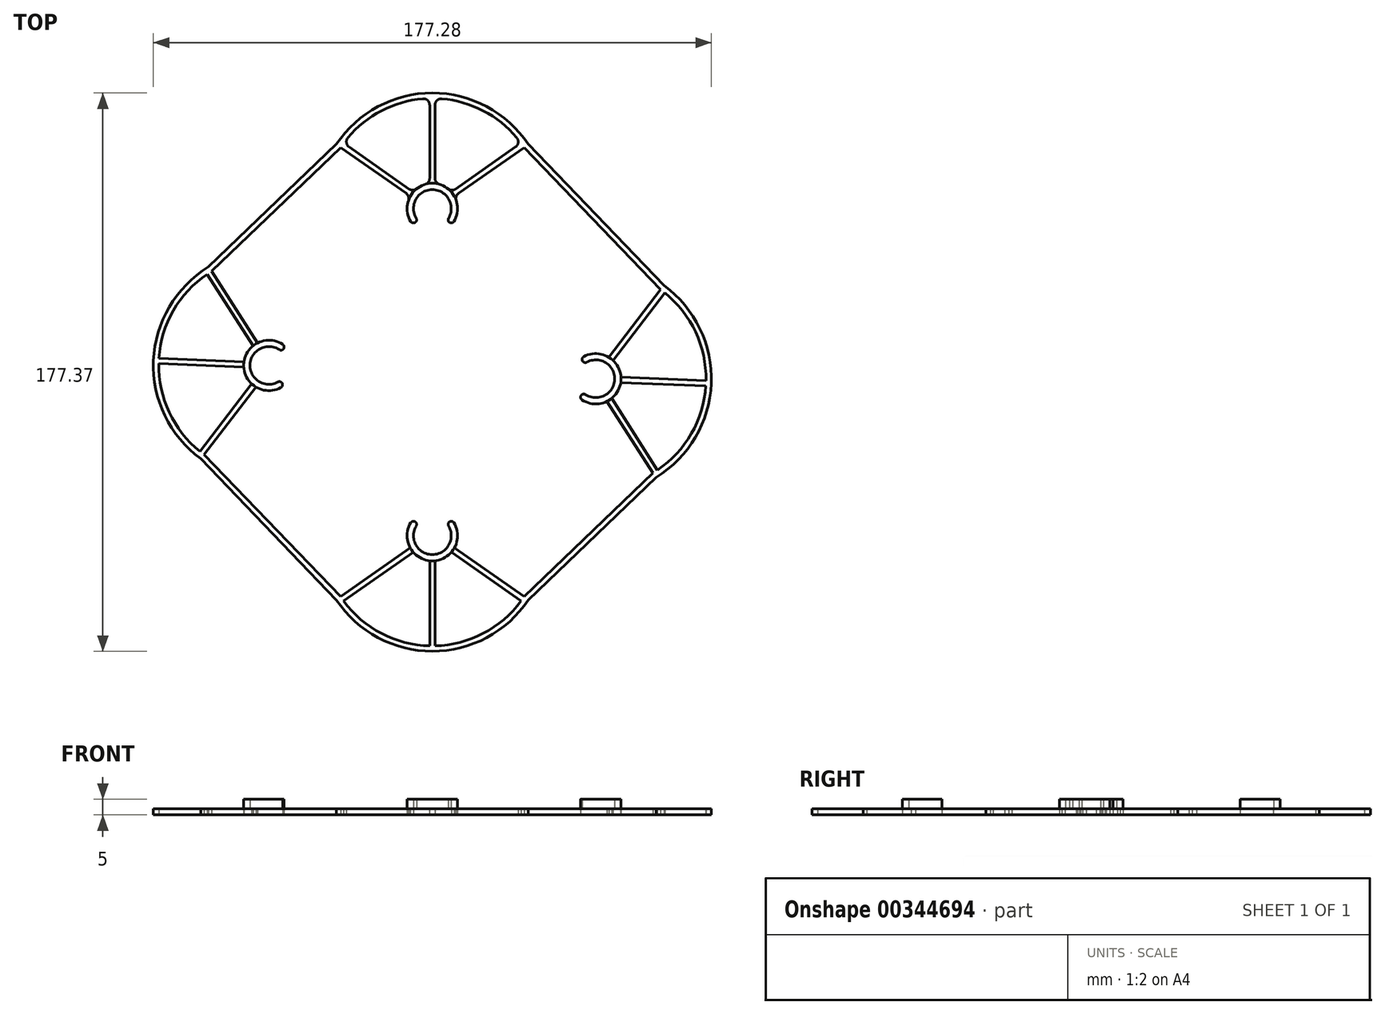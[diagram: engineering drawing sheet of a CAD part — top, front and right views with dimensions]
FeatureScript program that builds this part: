
annotation { "Feature Type Name" : "Feature", "Feature Type Description" : "" }
export const myFeature = defineFeature(function(context is Context, id is Id, definition is map)
    precondition{}
    {
        {
            var Q0;
            Q0=qCreatedBy(makeId("Top.planeOp"),FACE);
            var sketch = newSketch(context, id + "F0", { "sketchPlane" : qUnion([Q0])});
            skArc(sketch, "E0", {"start": v(5, -3.32) * mm, "mid": v(0, 6) * mm, "end": v(-5, -3.32) * mm});
            skArc(sketch, "E1", {"start": v(-7, 3.87) * mm, "mid": v(-7.85, -1.56) * mm, "end": v(-5, -6.24) * mm});
            skLineSegment(sketch, "E2", {"start": v(-7, 3.87) * mm, "end": v(-29.15, 19.37) * mm});
            skArc(sketch, "E3", {"start": v(28.17, 20.77) * mm, "mid": v(16.16, 31.05) * mm, "end": v(0.85, 34.99) * mm});
            skLineSegment(sketch, "E4", {"start": v(-6.03, 5.26) * mm, "end": v(-28.17, 20.77) * mm});
            skLineSegment(sketch, "E5", {"start": v(0, 0) * mm, "end": v(-28.67, 20.08) * mm, "construction": true});
            skLineSegment(sketch, "E6", {"start": v(0, 0) * mm, "end": v(0, 35) * mm, "construction": true});
            skLineSegment(sketch, "E7.MirrorCS", {"start": v(6.03, 5.26) * mm, "end": v(28.17, 20.77) * mm});
            skLineSegment(sketch, "E8.MirrorCS", {"start": v(7, 3.87) * mm, "end": v(29.15, 19.37) * mm});
            skLineSegment(sketch, "E9", {"start": v(-0.85, 7.95) * mm, "end": v(-0.85, 34.99) * mm});
            skLineSegment(sketch, "E10", {"start": v(0.85, 34.99) * mm, "end": v(0.85, 7.95) * mm});
            skArc(sketch, "E11", {"start": v(30.49, 20.43) * mm, "mid": v(0, 36.7) * mm, "end": v(-30.49, 20.43) * mm});
            skArc(sketch, "E12.trimOffspring", {"start": v(-0.85, 7.95) * mm, "mid": v(-3.7, 7.1) * mm, "end": v(-6.03, 5.26) * mm});
            skArc(sketch, "E13.trimOffspring", {"start": v(6.03, 5.26) * mm, "mid": v(3.7, 7.1) * mm, "end": v(0.85, 7.95) * mm});
            skArc(sketch, "E14.trimOffspring", {"start": v(-0.85, 34.99) * mm, "mid": v(-16.16, 31.05) * mm, "end": v(-28.17, 20.77) * mm});
            skPoint(sketch, "E15.middle", {"position": v(0, -9.2) * mm});
            skPoint(sketch, "E15.bottom.start.orphan", {"position": v(-4, -0.06) * mm});
            skPoint(sketch, "E16.orphan", {"position": v(4, 0.05) * mm});
            skArc(sketch, "E17.trimOffspring", {"start": v(5, -6.24) * mm, "mid": v(7.85, -1.56) * mm, "end": v(7, 3.87) * mm});
            skPoint(sketch, "E15.top.end.orphan", {"position": v(4, -18.32) * mm});
            skPoint(sketch, "E15.top.start.orphan", {"position": v(-4, -18.43) * mm});
            skLineSegment(sketch, "E18", {"start": v(0, 0) * mm, "end": v(51.94, -54.1) * mm, "construction": true});
            skLineSegment(sketch, "E19", {"start": v(51.94, -54.1) * mm, "end": v(0, -103.97) * mm, "construction": true});
            skLineSegment(sketch, "E20", {"start": v(0, -103.97) * mm, "end": v(-51.94, -49.86) * mm, "construction": true});
            skLineSegment(sketch, "E21", {"start": v(-51.94, -49.86) * mm, "end": v(0, 0) * mm, "construction": true});
            skLineSegment(sketch, "E22", {"start": v(0, 0) * mm, "end": v(0, -103.97) * mm, "construction": true});
            skLineSegment(sketch, "E23", {"start": v(51.94, -54.1) * mm, "end": v(-51.94, -49.86) * mm, "construction": true});
            skLineSegment(sketch, "E24", {"start": v(0, -51.98) * mm, "end": v(54.15, 0) * mm, "construction": true});
            skLineSegment(sketch, "E25.MirrorCS", {"start": v(48.42, -58.96) * mm, "end": v(45.5, -58.85) * mm});
            skLineSegment(sketch, "E26.MirrorCS", {"start": v(48.83, -48.97) * mm, "end": v(45.9, -48.85) * mm});
            skArc(sketch, "E27.MirrorCS", {"start": v(57.44, -48.3) * mm, "mid": v(59.18, -50.7) * mm, "end": v(59.92, -53.58) * mm});
            skArc(sketch, "E28.MirrorCS", {"start": v(59.85, -55.28) * mm, "mid": v(58.88, -58.08) * mm, "end": v(56.95, -60.34) * mm});
            skLineSegment(sketch, "E29.MirrorCS", {"start": v(55.52, -61.26) * mm, "end": v(70.1, -84.02) * mm});
            skLineSegment(sketch, "E30.MirrorCS", {"start": v(57.44, -48.3) * mm, "end": v(73.84, -26.8) * mm});
            skArc(sketch, "E31.MirrorCS", {"start": v(55.52, -61.26) * mm, "mid": v(50.07, -61.88) * mm, "end": v(45.5, -58.85) * mm});
            skPoint(sketch, "E32.MirrorP", {"position": v(51.71, -58.1) * mm});
            skLineSegment(sketch, "E33.MirrorCS", {"start": v(56.09, -47.26) * mm, "end": v(72.49, -25.77) * mm});
            skLineSegment(sketch, "E34.MirrorCS", {"start": v(56.95, -60.34) * mm, "end": v(71.54, -83.1) * mm});
            skArc(sketch, "E35.MirrorCS", {"start": v(73.6, -24.47) * mm, "mid": v(88.6, -55.6) * mm, "end": v(71.1, -85.4) * mm});
            skArc(sketch, "E36.MirrorCS", {"start": v(73.84, -26.8) * mm, "mid": v(83.62, -39.22) * mm, "end": v(86.94, -54.68) * mm});
            skLineSegment(sketch, "E37.MirrorCS", {"start": v(59.85, -55.28) * mm, "end": v(86.87, -56.38) * mm});
            skLineSegment(sketch, "E38.MirrorCS", {"start": v(86.94, -54.68) * mm, "end": v(59.92, -53.58) * mm});
            skArc(sketch, "E39.MirrorCS", {"start": v(48.83, -48.97) * mm, "mid": v(57.93, -54.35) * mm, "end": v(48.42, -58.96) * mm});
            skPoint(sketch, "E40.MirrorP", {"position": v(52.15, -50.1) * mm});
            skArc(sketch, "E41.MirrorCS", {"start": v(45.9, -48.85) * mm, "mid": v(50.7, -46.2) * mm, "end": v(56.09, -47.26) * mm});
            skArc(sketch, "E42.MirrorCS", {"start": v(86.87, -56.38) * mm, "mid": v(82.3, -71.52) * mm, "end": v(71.54, -83.1) * mm});
            skLineSegment(sketch, "E43", {"start": v(0, -51.98) * mm, "end": v(-83.37, 34.86) * mm, "construction": true});
            skArc(sketch, "E44.MirrorCS", {"start": v(-45.9, -55.11) * mm, "mid": v(-50.7, -57.77) * mm, "end": v(-56.09, -56.7) * mm});
            skLineSegment(sketch, "E45.MirrorCS", {"start": v(-48.83, -55) * mm, "end": v(-45.9, -55.11) * mm});
            skArc(sketch, "E46.MirrorCS", {"start": v(-57.44, -55.67) * mm, "mid": v(-59.18, -53.26) * mm, "end": v(-59.92, -50.39) * mm});
            skLineSegment(sketch, "E47.MirrorCS", {"start": v(-48.42, -45) * mm, "end": v(-45.5, -45.12) * mm});
            skArc(sketch, "E48.MirrorCS", {"start": v(-73.6, -79.5) * mm, "mid": v(-88.6, -48.36) * mm, "end": v(-71.1, -18.57) * mm});
            skArc(sketch, "E49.MirrorCS", {"start": v(-59.85, -48.69) * mm, "mid": v(-58.88, -45.88) * mm, "end": v(-56.95, -43.62) * mm});
            skArc(sketch, "E50.MirrorCS", {"start": v(-73.84, -77.17) * mm, "mid": v(-83.62, -64.74) * mm, "end": v(-86.94, -49.28) * mm});
            skPoint(sketch, "E51.MirrorP", {"position": v(-52.15, -53.86) * mm});
            skArc(sketch, "E52.MirrorCS", {"start": v(-86.87, -47.59) * mm, "mid": v(-82.3, -32.45) * mm, "end": v(-71.54, -20.86) * mm});
            skLineSegment(sketch, "E53.MirrorCS", {"start": v(-59.85, -48.69) * mm, "end": v(-86.87, -47.59) * mm});
            skPoint(sketch, "E54.MirrorP", {"position": v(-42.76, -50.24) * mm});
            skArc(sketch, "E55.MirrorCS", {"start": v(-48.83, -55) * mm, "mid": v(-57.93, -49.62) * mm, "end": v(-48.42, -45) * mm});
            skLineSegment(sketch, "E56.MirrorCS", {"start": v(-56.95, -43.62) * mm, "end": v(-71.54, -20.86) * mm});
            skArc(sketch, "E57.MirrorCS", {"start": v(-55.52, -42.7) * mm, "mid": v(-50.07, -42.08) * mm, "end": v(-45.5, -45.12) * mm});
            skLineSegment(sketch, "E58.MirrorCS", {"start": v(-56.09, -56.7) * mm, "end": v(-72.49, -78.2) * mm});
            skLineSegment(sketch, "E59.MirrorCS", {"start": v(-55.52, -42.7) * mm, "end": v(-70.1, -19.95) * mm});
            skPoint(sketch, "E60.MirrorP", {"position": v(-51.71, -45.87) * mm});
            skLineSegment(sketch, "E61.MirrorCS", {"start": v(-57.44, -55.67) * mm, "end": v(-73.84, -77.17) * mm});
            skLineSegment(sketch, "E62.MirrorCS", {"start": v(-86.94, -49.28) * mm, "end": v(-59.92, -50.39) * mm});
            skLineSegment(sketch, "E63.MirrorCS", {"start": v(-5, -100.65) * mm, "end": v(-5, -97.72) * mm});
            skArc(sketch, "E64.MirrorCS", {"start": v(0.85, -111.92) * mm, "mid": v(3.7, -111.06) * mm, "end": v(6.03, -109.23) * mm});
            skArc(sketch, "E65.MirrorCS", {"start": v(-6.03, -109.23) * mm, "mid": v(-3.7, -111.06) * mm, "end": v(-0.85, -111.92) * mm});
            skLineSegment(sketch, "E66.MirrorCS", {"start": v(5, -100.65) * mm, "end": v(5, -97.72) * mm});
            skLineSegment(sketch, "E67.MirrorCS", {"start": v(-6.03, -109.23) * mm, "end": v(-28.17, -124.73) * mm});
            skArc(sketch, "E68.MirrorCS", {"start": v(-30.49, -124.4) * mm, "mid": v(0, -140.67) * mm, "end": v(30.49, -124.4) * mm});
            skArc(sketch, "E69.MirrorCS", {"start": v(-5, -97.72) * mm, "mid": v(-7.85, -102.41) * mm, "end": v(-7, -107.83) * mm});
            skArc(sketch, "E70.MirrorCS", {"start": v(-5, -100.65) * mm, "mid": v(0, -109.97) * mm, "end": v(5, -100.65) * mm});
            skArc(sketch, "E71.MirrorCS", {"start": v(-28.17, -124.73) * mm, "mid": v(-16.16, -135.01) * mm, "end": v(-0.85, -138.96) * mm});
            skPoint(sketch, "E72.MirrorP", {"position": v(-4, -104.01) * mm});
            skLineSegment(sketch, "E73.MirrorCS", {"start": v(-7, -107.83) * mm, "end": v(-29.15, -123.34) * mm});
            skLineSegment(sketch, "E74.MirrorCS", {"start": v(0.85, -111.92) * mm, "end": v(0.85, -138.96) * mm});
            skArc(sketch, "E75.MirrorCS", {"start": v(7, -107.83) * mm, "mid": v(7.85, -102.41) * mm, "end": v(5, -97.72) * mm});
            skPoint(sketch, "E76.MirrorP", {"position": v(4, -103.9) * mm});
            skLineSegment(sketch, "E77.MirrorCS", {"start": v(-0.85, -138.96) * mm, "end": v(-0.85, -111.92) * mm});
            skLineSegment(sketch, "E78.MirrorCS", {"start": v(7, -107.83) * mm, "end": v(29.15, -123.34) * mm});
            skLineSegment(sketch, "E79.MirrorCS", {"start": v(6.03, -109.23) * mm, "end": v(28.17, -124.73) * mm});
            skArc(sketch, "E80.MirrorCS", {"start": v(0.85, -138.96) * mm, "mid": v(16.16, -135.01) * mm, "end": v(28.17, -124.73) * mm});
            skLineSegment(sketch, "E81", {"start": v(73.6, -24.47) * mm, "end": v(30.49, 20.43) * mm});
            skLineSegment(sketch, "E82", {"start": v(72.49, -25.77) * mm, "end": v(29.15, 19.37) * mm});
            skLineSegment(sketch, "E83", {"start": v(71.1, -85.4) * mm, "end": v(30.49, -124.4) * mm});
            skLineSegment(sketch, "E84", {"start": v(70.1, -84.02) * mm, "end": v(29.15, -123.34) * mm});
            skLineSegment(sketch, "E85", {"start": v(-30.49, -124.4) * mm, "end": v(-73.6, -79.5) * mm});
            skLineSegment(sketch, "E86", {"start": v(-29.15, -123.34) * mm, "end": v(-72.49, -78.2) * mm});
            skLineSegment(sketch, "E87", {"start": v(-71.1, -18.57) * mm, "end": v(-30.49, 20.43) * mm});
            skLineSegment(sketch, "E88", {"start": v(-29.15, 19.37) * mm, "end": v(-70.1, -19.95) * mm});
            skLineSegment(sketch, "E89", {"start": v(-5, -3.32) * mm, "end": v(-5, -6.24) * mm});
            skLineSegment(sketch, "E90", {"start": v(5, -3.32) * mm, "end": v(5, -6.24) * mm});
            skSolve(sketch);
        }
        {
            var Q0;
            Q0 = qSketchRegion(id + "F0", true);
            extrude(context, id + "F1", {"entities" : qUnion([Q0]), "depth" : 2 * mm});
        }
        {
            var Q0;
            Q0=makeQuery(id+"F1.opExtrude","SWEPT_EDGE",EDGE,{"disambiguationData":[OSD([sQuery(id+"F0.wireOp",EDGE,"E0"),sQuery(id+"F0.wireOp",EDGE,"E89")])]});
            var Q1;
            Q1=makeQuery(id+"F1.opExtrude","SWEPT_EDGE",EDGE,{"disambiguationData":[OSD([sQuery(id+"F0.wireOp",EDGE,"E1"),sQuery(id+"F0.wireOp",EDGE,"E89")])]});
            var Q2;
            Q2=makeQuery(id+"F1.opExtrude","SWEPT_EDGE",EDGE,{"disambiguationData":[OSD([sQuery(id+"F0.wireOp",EDGE,"E0"),sQuery(id+"F0.wireOp",EDGE,"E90")])]});
            var Q3;
            Q3=makeQuery(id+"F1.opExtrude","SWEPT_EDGE",EDGE,{"disambiguationData":[OSD([sQuery(id+"F0.wireOp",EDGE,"E17.trimOffspring"),sQuery(id+"F0.wireOp",EDGE,"E90")])]});
            var Q4;
            Q4=makeQuery(id+"F1.opExtrude","SWEPT_EDGE",EDGE,{"disambiguationData":[OSD([sQuery(id+"F0.wireOp",EDGE,"E26.MirrorCS"),sQuery(id+"F0.wireOp",EDGE,"E39.MirrorCS")])]});
            var Q5;
            Q5=makeQuery(id+"F1.opExtrude","SWEPT_EDGE",EDGE,{"disambiguationData":[OSD([sQuery(id+"F0.wireOp",EDGE,"E26.MirrorCS"),sQuery(id+"F0.wireOp",EDGE,"E41.MirrorCS")])]});
            var Q6;
            Q6=makeQuery(id+"F1.opExtrude","SWEPT_EDGE",EDGE,{"disambiguationData":[OSD([sQuery(id+"F0.wireOp",EDGE,"E25.MirrorCS"),sQuery(id+"F0.wireOp",EDGE,"E39.MirrorCS")])]});
            var Q7;
            Q7=makeQuery(id+"F1.opExtrude","SWEPT_EDGE",EDGE,{"disambiguationData":[OSD([sQuery(id+"F0.wireOp",EDGE,"E25.MirrorCS"),sQuery(id+"F0.wireOp",EDGE,"E31.MirrorCS")])]});
            var Q8;
            Q8=makeQuery(id+"F1.opExtrude","SWEPT_EDGE",EDGE,{"disambiguationData":[OSD([sQuery(id+"F0.wireOp",EDGE,"E66.MirrorCS"),sQuery(id+"F0.wireOp",EDGE,"E70.MirrorCS")])]});
            var Q9;
            Q9=makeQuery(id+"F1.opExtrude","SWEPT_EDGE",EDGE,{"disambiguationData":[OSD([sQuery(id+"F0.wireOp",EDGE,"E66.MirrorCS"),sQuery(id+"F0.wireOp",EDGE,"E75.MirrorCS")])]});
            var Q10;
            Q10=makeQuery(id+"F1.opExtrude","SWEPT_EDGE",EDGE,{"disambiguationData":[OSD([sQuery(id+"F0.wireOp",EDGE,"E63.MirrorCS"),sQuery(id+"F0.wireOp",EDGE,"E69.MirrorCS")])]});
            var Q11;
            Q11=makeQuery(id+"F1.opExtrude","SWEPT_EDGE",EDGE,{"disambiguationData":[OSD([sQuery(id+"F0.wireOp",EDGE,"E63.MirrorCS"),sQuery(id+"F0.wireOp",EDGE,"E70.MirrorCS")])]});
            var Q12;
            Q12=makeQuery(id+"F1.opExtrude","SWEPT_EDGE",EDGE,{"disambiguationData":[OSD([sQuery(id+"F0.wireOp",EDGE,"E45.MirrorCS"),sQuery(id+"F0.wireOp",EDGE,"E55.MirrorCS")])]});
            var Q13;
            Q13=makeQuery(id+"F1.opExtrude","SWEPT_EDGE",EDGE,{"disambiguationData":[OSD([sQuery(id+"F0.wireOp",EDGE,"E44.MirrorCS"),sQuery(id+"F0.wireOp",EDGE,"E45.MirrorCS")])]});
            var Q14;
            Q14=makeQuery(id+"F1.opExtrude","SWEPT_EDGE",EDGE,{"disambiguationData":[OSD([sQuery(id+"F0.wireOp",EDGE,"E47.MirrorCS"),sQuery(id+"F0.wireOp",EDGE,"E55.MirrorCS")])]});
            var Q15;
            Q15=makeQuery(id+"F1.opExtrude","SWEPT_EDGE",EDGE,{"disambiguationData":[OSD([sQuery(id+"F0.wireOp",EDGE,"E47.MirrorCS"),sQuery(id+"F0.wireOp",EDGE,"E57.MirrorCS")])]});
            fillet(context, id + "F2", {"entities" : qUnion([Q0, Q1, Q2, Q3, Q4, Q5, Q6, Q7, Q8, Q9, Q10, Q11, Q12, Q13, Q14, Q15]), "radius" : 1 * mm, "tangentPropagation" : true, "allowEdgeOverflow" : false});
        }
        {
            var Q0;
            Q0=makeQuery(id+"F1.opExtrude","SWEPT_EDGE",EDGE,{"disambiguationData":[OSD([sQuery(id+"F0.wireOp",EDGE,"E7.MirrorCS"),sQuery(id+"F0.wireOp",EDGE,"E13.trimOffspring")])]});
            var Q1;
            Q1=makeQuery(id+"F1.opExtrude","SWEPT_EDGE",EDGE,{"disambiguationData":[OSD([sQuery(id+"F0.wireOp",EDGE,"E10"),sQuery(id+"F0.wireOp",EDGE,"E13.trimOffspring")])]});
            var Q2;
            Q2=makeQuery(id+"F1.opExtrude","SWEPT_EDGE",EDGE,{"disambiguationData":[OSD([sQuery(id+"F0.wireOp",EDGE,"E8.MirrorCS"),sQuery(id+"F0.wireOp",EDGE,"E17.trimOffspring")])]});
            var Q3;
            Q3=makeQuery(id+"F1.opExtrude","SWEPT_EDGE",EDGE,{"disambiguationData":[OSD([sQuery(id+"F0.wireOp",EDGE,"E9"),sQuery(id+"F0.wireOp",EDGE,"E12.trimOffspring")])]});
            var Q4;
            Q4=makeQuery(id+"F1.opExtrude","SWEPT_EDGE",EDGE,{"disambiguationData":[OSD([sQuery(id+"F0.wireOp",EDGE,"E1"),sQuery(id+"F0.wireOp",EDGE,"E2")])]});
            var Q5;
            Q5=makeQuery(id+"F1.opExtrude","SWEPT_EDGE",EDGE,{"disambiguationData":[OSD([sQuery(id+"F0.wireOp",EDGE,"E4"),sQuery(id+"F0.wireOp",EDGE,"E12.trimOffspring")])]});
            var Q6;
            Q6=makeQuery(id+"F1.opExtrude","SWEPT_EDGE",EDGE,{"disambiguationData":[OSD([sQuery(id+"F0.wireOp",EDGE,"E3"),sQuery(id+"F0.wireOp",EDGE,"E7.MirrorCS")])]});
            var Q7;
            Q7=makeQuery(id+"F1.opExtrude","SWEPT_EDGE",EDGE,{"disambiguationData":[OSD([sQuery(id+"F0.wireOp",EDGE,"E4"),sQuery(id+"F0.wireOp",EDGE,"E14.trimOffspring")])]});
            var Q8;
            Q8=makeQuery(id+"F1.opExtrude","SWEPT_EDGE",EDGE,{"disambiguationData":[OSD([sQuery(id+"F0.wireOp",EDGE,"E9"),sQuery(id+"F0.wireOp",EDGE,"E14.trimOffspring")])]});
            var Q9;
            Q9=makeQuery(id+"F1.opExtrude","SWEPT_EDGE",EDGE,{"disambiguationData":[OSD([sQuery(id+"F0.wireOp",EDGE,"E3"),sQuery(id+"F0.wireOp",EDGE,"E10")])]});
            fillet(context, id + "F3", {"entities" : qUnion([Q0, Q1, Q2, Q3, Q4, Q5, Q6, Q7, Q8, Q9]), "radius" : 2 * mm, "tangentPropagation" : true, "allowEdgeOverflow" : false});
        }
        {
            var Q0;
            Q0=makeQuery(id+"F1.opExtrude","CAP_FACE",FACE,{"disambiguationData":[OSD([sQuery(id+"F0.wireOp",EDGE,"E0"),sQuery(id+"F0.wireOp",EDGE,"E1"),sQuery(id+"F0.wireOp",EDGE,"E2"),sQuery(id+"F0.wireOp",EDGE,"E3"),sQuery(id+"F0.wireOp",EDGE,"E4"),sQuery(id+"F0.wireOp",EDGE,"E7.MirrorCS"),sQuery(id+"F0.wireOp",EDGE,"E8.MirrorCS"),sQuery(id+"F0.wireOp",EDGE,"E9"),sQuery(id+"F0.wireOp",EDGE,"E10"),sQuery(id+"F0.wireOp",EDGE,"E11"),sQuery(id+"F0.wireOp",EDGE,"E12.trimOffspring"),sQuery(id+"F0.wireOp",EDGE,"E13.trimOffspring"),sQuery(id+"F0.wireOp",EDGE,"E14.trimOffspring"),sQuery(id+"F0.wireOp",EDGE,"E15.left"),sQuery(id+"F0.wireOp",EDGE,"E15.right"),sQuery(id+"F0.wireOp",EDGE,"E17.trimOffspring"),sQuery(id+"F0.wireOp",EDGE,"E25.MirrorCS"),sQuery(id+"F0.wireOp",EDGE,"E26.MirrorCS"),sQuery(id+"F0.wireOp",EDGE,"E27.MirrorCS"),sQuery(id+"F0.wireOp",EDGE,"E28.MirrorCS"),sQuery(id+"F0.wireOp",EDGE,"E29.MirrorCS"),sQuery(id+"F0.wireOp",EDGE,"E30.MirrorCS"),sQuery(id+"F0.wireOp",EDGE,"E31.MirrorCS"),sQuery(id+"F0.wireOp",EDGE,"E33.MirrorCS"),sQuery(id+"F0.wireOp",EDGE,"E34.MirrorCS"),sQuery(id+"F0.wireOp",EDGE,"E35.MirrorCS"),sQuery(id+"F0.wireOp",EDGE,"E36.MirrorCS"),sQuery(id+"F0.wireOp",EDGE,"E37.MirrorCS"),sQuery(id+"F0.wireOp",EDGE,"E38.MirrorCS"),sQuery(id+"F0.wireOp",EDGE,"E39.MirrorCS"),sQuery(id+"F0.wireOp",EDGE,"E41.MirrorCS"),sQuery(id+"F0.wireOp",EDGE,"E42.MirrorCS"),sQuery(id+"F0.wireOp",EDGE,"E44.MirrorCS"),sQuery(id+"F0.wireOp",EDGE,"E45.MirrorCS"),sQuery(id+"F0.wireOp",EDGE,"E46.MirrorCS"),sQuery(id+"F0.wireOp",EDGE,"E47.MirrorCS"),sQuery(id+"F0.wireOp",EDGE,"E48.MirrorCS"),sQuery(id+"F0.wireOp",EDGE,"E49.MirrorCS"),sQuery(id+"F0.wireOp",EDGE,"E50.MirrorCS"),sQuery(id+"F0.wireOp",EDGE,"E52.MirrorCS"),sQuery(id+"F0.wireOp",EDGE,"E53.MirrorCS"),sQuery(id+"F0.wireOp",EDGE,"E55.MirrorCS"),sQuery(id+"F0.wireOp",EDGE,"E56.MirrorCS"),sQuery(id+"F0.wireOp",EDGE,"E57.MirrorCS"),sQuery(id+"F0.wireOp",EDGE,"E58.MirrorCS"),sQuery(id+"F0.wireOp",EDGE,"E59.MirrorCS"),sQuery(id+"F0.wireOp",EDGE,"E61.MirrorCS"),sQuery(id+"F0.wireOp",EDGE,"E62.MirrorCS"),sQuery(id+"F0.wireOp",EDGE,"E63.MirrorCS"),sQuery(id+"F0.wireOp",EDGE,"E64.MirrorCS"),sQuery(id+"F0.wireOp",EDGE,"E65.MirrorCS"),sQuery(id+"F0.wireOp",EDGE,"E66.MirrorCS"),sQuery(id+"F0.wireOp",EDGE,"E67.MirrorCS"),sQuery(id+"F0.wireOp",EDGE,"E68.MirrorCS"),sQuery(id+"F0.wireOp",EDGE,"E69.MirrorCS"),sQuery(id+"F0.wireOp",EDGE,"E70.MirrorCS"),sQuery(id+"F0.wireOp",EDGE,"E71.MirrorCS"),sQuery(id+"F0.wireOp",EDGE,"E73.MirrorCS"),sQuery(id+"F0.wireOp",EDGE,"E74.MirrorCS"),sQuery(id+"F0.wireOp",EDGE,"E75.MirrorCS"),sQuery(id+"F0.wireOp",EDGE,"E77.MirrorCS"),sQuery(id+"F0.wireOp",EDGE,"E78.MirrorCS"),sQuery(id+"F0.wireOp",EDGE,"E79.MirrorCS"),sQuery(id+"F0.wireOp",EDGE,"E80.MirrorCS"),sQuery(id+"F0.wireOp",EDGE,"E81"),sQuery(id+"F0.wireOp",EDGE,"E82"),sQuery(id+"F0.wireOp",EDGE,"E83"),sQuery(id+"F0.wireOp",EDGE,"E84"),sQuery(id+"F0.wireOp",EDGE,"E85"),sQuery(id+"F0.wireOp",EDGE,"E86"),sQuery(id+"F0.wireOp",EDGE,"E87"),sQuery(id+"F0.wireOp",EDGE,"E88")])],"isStart":false});
            var sketch = newSketch(context, id + "F4", { "sketchPlane" : qUnion([Q0])});
            skLineSegment(sketch, "E91.0", {"start": v(73.6, -24.47) * mm, "end": v(30.49, 20.43) * mm});
            skArc(sketch, "E92.0", {"start": v(73.6, -24.47) * mm, "mid": v(88.6, -55.6) * mm, "end": v(71.1, -85.4) * mm});
            skLineSegment(sketch, "E93.0", {"start": v(71.1, -85.4) * mm, "end": v(30.49, -124.4) * mm});
            skArc(sketch, "E94.0", {"start": v(-30.49, -124.4) * mm, "mid": v(0, -140.67) * mm, "end": v(30.49, -124.4) * mm});
            skLineSegment(sketch, "E95.0", {"start": v(-30.49, -124.4) * mm, "end": v(-73.6, -79.5) * mm});
            skArc(sketch, "E96.0", {"start": v(-73.6, -79.5) * mm, "mid": v(-88.6, -48.36) * mm, "end": v(-71.1, -18.57) * mm});
            skLineSegment(sketch, "E97.0", {"start": v(-71.1, -18.57) * mm, "end": v(-30.49, 20.43) * mm});
            skArc(sketch, "E98.0", {"start": v(30.49, 20.43) * mm, "mid": v(0, 36.7) * mm, "end": v(-30.49, 20.43) * mm});
            skArc(sketch, "E99.0", {"start": v(72.7, -25.5) * mm, "mid": v(87.26, -55.56) * mm, "end": v(70.28, -84.33) * mm});
            skLineSegment(sketch, "E99.1", {"start": v(70.28, -84.33) * mm, "end": v(29.45, -123.52) * mm});
            skLineSegment(sketch, "E99.2", {"start": v(72.7, -25.5) * mm, "end": v(29.43, 19.58) * mm});
            skArc(sketch, "E99.3", {"start": v(-29.43, -123.55) * mm, "mid": v(0.01, -139.32) * mm, "end": v(29.45, -123.52) * mm});
            skArc(sketch, "E99.4", {"start": v(29.43, 19.58) * mm, "mid": v(-0.01, 35.35) * mm, "end": v(-29.45, 19.56) * mm});
            skLineSegment(sketch, "E99.5", {"start": v(-70.28, -19.64) * mm, "end": v(-29.45, 19.56) * mm});
            skArc(sketch, "E99.6", {"start": v(-72.7, -78.47) * mm, "mid": v(-87.26, -48.4) * mm, "end": v(-70.28, -19.64) * mm});
            skLineSegment(sketch, "E99.7", {"start": v(-29.43, -123.55) * mm, "end": v(-72.7, -78.47) * mm});
            skSolve(sketch);
        }
        {
            var Q0;
            Q0=makeQuery(id+"F4.imprint","IMPRINT",FACE,{"disambiguationData":[TD([[makeQuery(id+"F4.imprint","IMPRINT",EDGE,{"derivedFrom":sQuery(id+"F4.wireOp",EDGE,"E99.0")}),-1.0]])]});
            var sketch = newSketch(context, id + "F5", { "sketchPlane" : qUnion([Q0])});
            skArc(sketch, "E100.0", {"start": v(-49.06, -55.13) * mm, "mid": v(-57.93, -49.62) * mm, "end": v(-48.64, -44.85) * mm, "construction": true});
            skArc(sketch, "E101.0", {"start": v(-48.64, -44.85) * mm, "mid": v(-47.26, -44.56) * mm, "end": v(-47.54, -43.18) * mm});
            skPoint(sketch, "E102.0", {"position": v(-48.1, -56.88) * mm});
            skArc(sketch, "E103.0", {"start": v(-48.1, -56.88) * mm, "mid": v(-47.7, -55.52) * mm, "end": v(-49.06, -55.13) * mm});
            skArc(sketch, "E104.0", {"start": v(-5.14, -100.88) * mm, "mid": v(0, -109.97) * mm, "end": v(5.14, -100.88) * mm, "construction": true});
            skArc(sketch, "E105.0", {"start": v(6.86, -99.85) * mm, "mid": v(5.48, -99.5) * mm, "end": v(5.14, -100.88) * mm});
            skArc(sketch, "E106.0", {"start": v(-5.14, -100.88) * mm, "mid": v(-5.48, -99.5) * mm, "end": v(-6.86, -99.85) * mm});
            skArc(sketch, "E107.0", {"start": v(49.06, -48.84) * mm, "mid": v(57.93, -54.35) * mm, "end": v(48.64, -59.12) * mm, "construction": true});
            skArc(sketch, "E108.0", {"start": v(48.64, -59.12) * mm, "mid": v(47.26, -59.4) * mm, "end": v(47.54, -60.79) * mm});
            skArc(sketch, "E109.0", {"start": v(48.1, -47.08) * mm, "mid": v(47.7, -48.44) * mm, "end": v(49.06, -48.84) * mm});
            skArc(sketch, "E110.0", {"start": v(5.14, -3.1) * mm, "mid": v(0, 6) * mm, "end": v(-5.14, -3.1) * mm, "construction": true});
            skArc(sketch, "E111.0", {"start": v(5.14, -3.1) * mm, "mid": v(5.48, -4.46) * mm, "end": v(6.86, -4.12) * mm});
            skArc(sketch, "E112.0", {"start": v(-6.86, -4.12) * mm, "mid": v(-5.48, -4.46) * mm, "end": v(-5.14, -3.1) * mm});
            skArc(sketch, "E113", {"start": v(5.14, -3.1) * mm, "mid": v(0, 6) * mm, "end": v(-5.14, -3.1) * mm});
            skArc(sketch, "E114", {"start": v(6.86, -4.12) * mm, "mid": v(0, 8) * mm, "end": v(-6.86, -4.12) * mm});
            skArc(sketch, "E115", {"start": v(48.64, -59.12) * mm, "mid": v(57.93, -54.35) * mm, "end": v(49.06, -48.84) * mm});
            skArc(sketch, "E116", {"start": v(47.54, -60.79) * mm, "mid": v(59.93, -54.43) * mm, "end": v(48.1, -47.08) * mm});
            skArc(sketch, "E117", {"start": v(-5.14, -100.88) * mm, "mid": v(0, -109.97) * mm, "end": v(5.14, -100.88) * mm});
            skArc(sketch, "E118", {"start": v(-6.86, -99.85) * mm, "mid": v(0, -111.97) * mm, "end": v(6.86, -99.85) * mm});
            skArc(sketch, "E119", {"start": v(-48.64, -44.85) * mm, "mid": v(-57.93, -49.62) * mm, "end": v(-49.06, -55.13) * mm});
            skArc(sketch, "E120", {"start": v(-47.54, -43.18) * mm, "mid": v(-59.93, -49.54) * mm, "end": v(-48.1, -56.88) * mm});
            skSolve(sketch);
        }
        {
            var Q0;
            Q0 = qSketchRegion(id + "F5", true);
            extrude(context, id + "F6", {"entities" : qUnion([Q0]), "operationType" : NewBodyOperationType.ADD, "depth" : 3 * mm});
        }
    });
